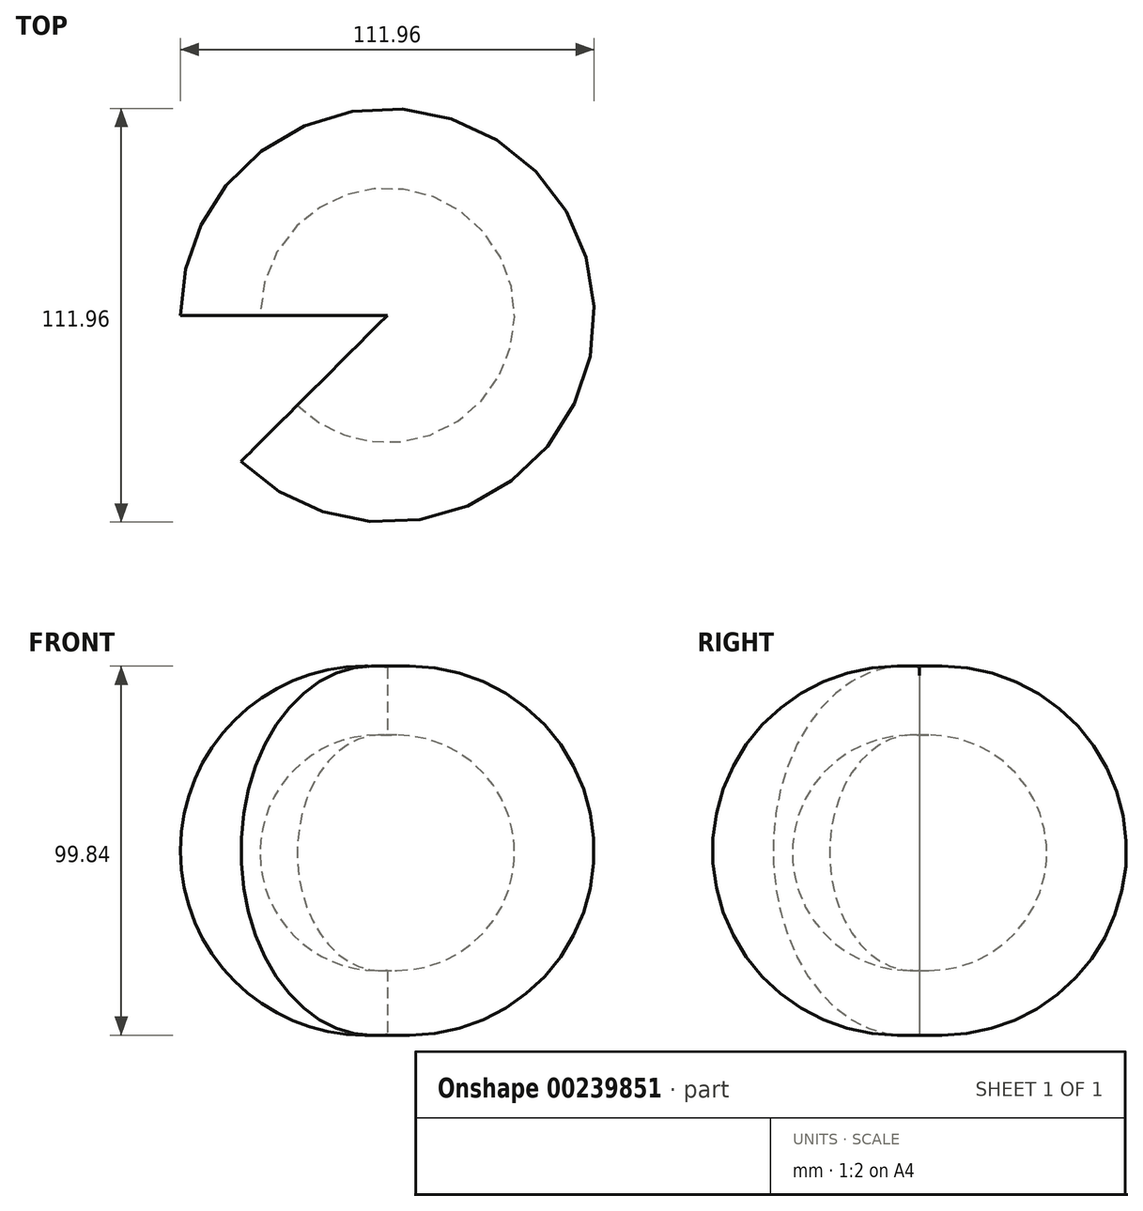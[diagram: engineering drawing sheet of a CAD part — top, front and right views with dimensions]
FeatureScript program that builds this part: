
annotation { "Feature Type Name" : "Feature", "Feature Type Description" : "" }
export const myFeature = defineFeature(function(context is Context, id is Id, definition is map)
    precondition{}
    {
        {
            var Q0;
            Q0=qCreatedBy(makeId("Front.planeOp"),FACE);
            var sketch = newSketch(context, id + "F0", { "sketchPlane" : qUnion([Q0])});
            skLineSegment(sketch, "E0", {"start": v(0, 52.61) * mm, "end": v(0, 34.25) * mm});
            skLineSegment(sketch, "E1", {"start": v(0, -29.3) * mm, "end": v(0, -46.5) * mm});
            skArc(sketch, "E2", {"start": v(0, 34.25) * mm, "mid": v(-34.42, 2.48) * mm, "end": v(0, -29.3) * mm});
            skArc(sketch, "E3", {"start": v(0, 52.61) * mm, "mid": v(-55.98, 3.06) * mm, "end": v(0, -46.5) * mm});
            skSolve(sketch);
        }
        {
            var Q0;
            Q0=makeQuery(id+"F0.imprint","IMPRINT",FACE,{"disambiguationData":[TD([[makeQuery(id+"F0.imprint","IMPRINT",EDGE,{"derivedFrom":sQuery(id+"F0.wireOp",EDGE,"E0")}),-1.0]])]});
            var Q1;
            Q1=sQuery(id+"F0.wireOp",EDGE,"E0");
            revolve(context, id + "F1", {"entities" : qUnion([Q0]), "axis" : qUnion([Q1]), "revolveType" : RevolveType.ONE_DIRECTION, "angle" : 315 * degree});
        }
    });
